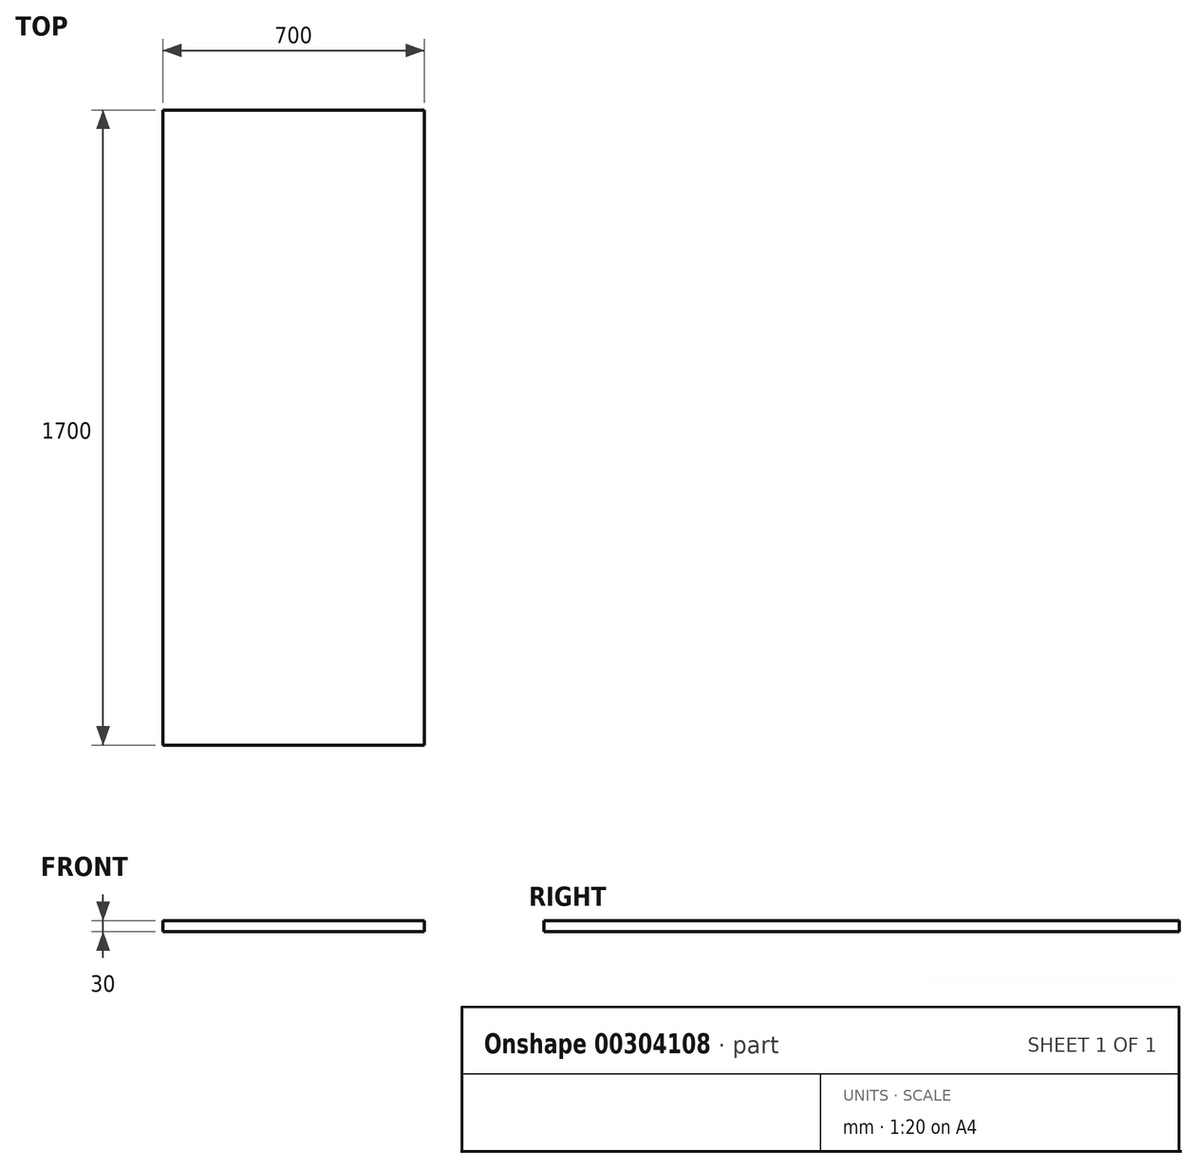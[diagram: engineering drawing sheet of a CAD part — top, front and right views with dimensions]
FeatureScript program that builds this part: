
annotation { "Feature Type Name" : "Feature", "Feature Type Description" : "" }
export const myFeature = defineFeature(function(context is Context, id is Id, definition is map)
    precondition{}
    {
        {
            var Q0;
            Q0=qCreatedBy(makeId("Top.planeOp"),FACE);
            var sketch = newSketch(context, id + "F0", { "sketchPlane" : qUnion([Q0])});
            skLineSegment(sketch, "E0.bottom", {"start": v(-398.7, 850.1) * mm, "end": v(301.3, 850.1) * mm});
            skLineSegment(sketch, "E0.top", {"start": v(-398.7, -849.9) * mm, "end": v(301.3, -849.9) * mm});
            skLineSegment(sketch, "E0.left", {"start": v(-398.7, 850.1) * mm, "end": v(-398.7, -849.9) * mm});
            skLineSegment(sketch, "E0.right", {"start": v(301.3, 850.1) * mm, "end": v(301.3, -849.9) * mm});
            skSolve(sketch);
        }
        {
            var Q0;
            Q0=makeQuery(id+"F0.imprint","IMPRINT",FACE,{"disambiguationData":[TD([[makeQuery(id+"F0.imprint","IMPRINT",EDGE,{"derivedFrom":sQuery(id+"F0.wireOp",EDGE,"E0.bottom")}),-1.0]])]});
            extrude(context, id + "F1", {"entities" : qUnion([Q0]), "depth" : 30 * mm, "offsetDistance" : 25 * mm});
        }
    });
